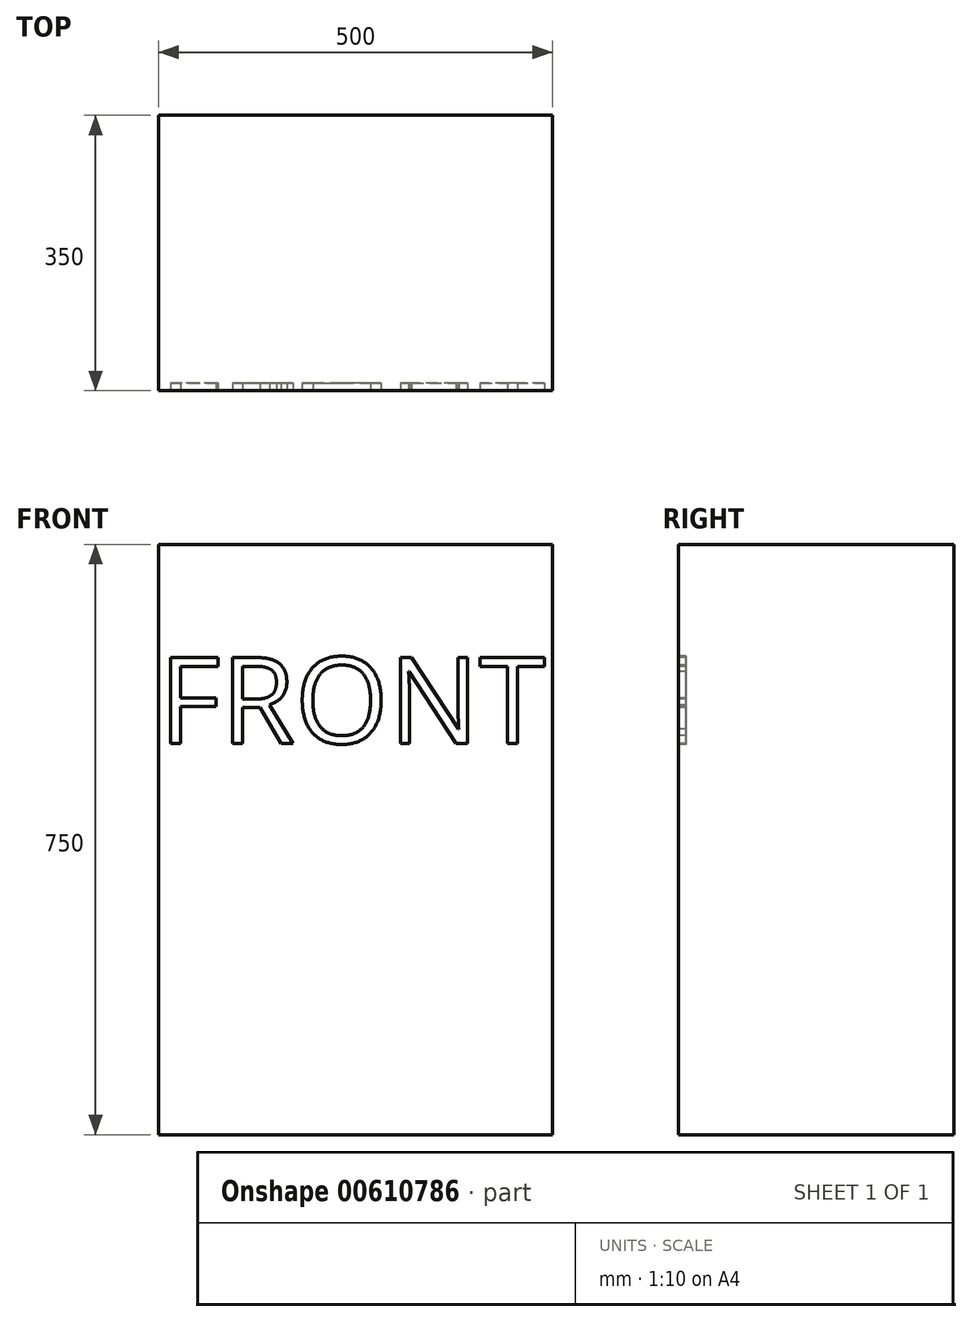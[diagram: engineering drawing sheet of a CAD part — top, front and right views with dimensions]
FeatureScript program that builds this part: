
annotation { "Feature Type Name" : "Feature", "Feature Type Description" : "" }
export const myFeature = defineFeature(function(context is Context, id is Id, definition is map)
    precondition{}
    {
        {
            var Q0;
            Q0=qCreatedBy(makeId("Top.planeOp"),FACE);
            var sketch = newSketch(context, id + "F0", { "sketchPlane" : qUnion([Q0])});
            skLineSegment(sketch, "E0.bottom", {"start": v(500, 350) * mm, "end": v(0, 350) * mm});
            skLineSegment(sketch, "E0.top", {"start": v(500, 0) * mm, "end": v(0, 0) * mm});
            skLineSegment(sketch, "E0.left", {"start": v(500, 350) * mm, "end": v(500, 0) * mm});
            skLineSegment(sketch, "E0.right", {"start": v(0, 350) * mm, "end": v(0, 0) * mm});
            skSolve(sketch);
        }
        {
            var Q0;
            Q0=makeQuery(id+"F0.imprint","IMPRINT",FACE,{"disambiguationData":[TD([[makeQuery(id+"F0.imprint","IMPRINT",EDGE,{"derivedFrom":sQuery(id+"F0.wireOp",EDGE,"E0.bottom")}),1.0]])]});
            extrude(context, id + "F1", {"entities" : qUnion([Q0]), "depth" : 750 * mm, "offsetDistance" : 25.4 * mm});
        }
        {
            var Q0;
            Q0=makeQuery(id+"F1.opExtrude","SWEPT_FACE",FACE,{"disambiguationData":[OSD([sQuery(id+"F0.wireOp",EDGE,"E0.top")])]});
            var sketch = newSketch(context, id + "F2", { "sketchPlane" : qUnion([Q0])});
            skText(sketch, "E1", { "text": "FRONT", "fontName": "OpenSans-Regular.ttf"});
            const initialGuessF2  = {"E1": [0, 0.4972, 1, 0, 0.1099]};
            skSetInitialGuess(sketch, initialGuessF2);
            skSolve(sketch);
        }
        {
            var Q0;
            Q0 = qSketchRegion(id + "F2", true);
            extrude(context, id + "F3", {"entities" : qUnion([Q0]), "operationType" : NewBodyOperationType.REMOVE, "oppositeDirection" : true, "depth" : 10 * mm, "offsetDistance" : 25 * mm});
        }
    });
